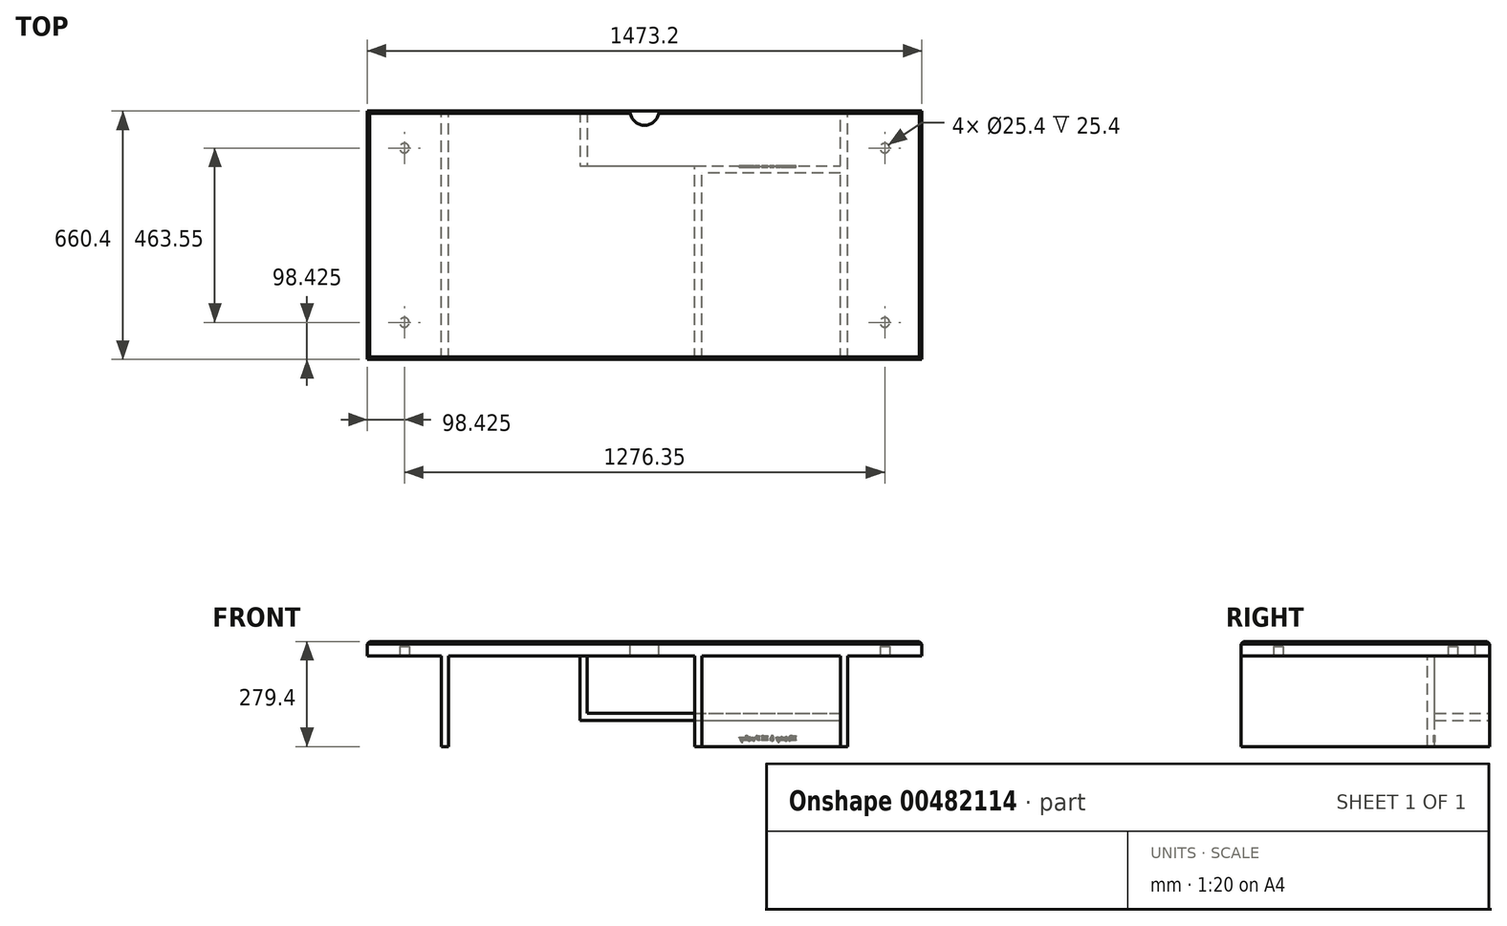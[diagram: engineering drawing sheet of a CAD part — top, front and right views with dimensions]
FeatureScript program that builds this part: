
annotation { "Feature Type Name" : "Feature", "Feature Type Description" : "" }
export const myFeature = defineFeature(function(context is Context, id is Id, definition is map)
    precondition{}
    {
        {
            var Q0;
            Q0=qCreatedBy(makeId("Top.planeOp"),FACE);
            var sketch = newSketch(context, id + "F0", { "sketchPlane" : qUnion([Q0])});
            skLineSegment(sketch, "E0.bottom", {"start": v(-736.6, 330.2) * mm, "end": v(736.6, 330.2) * mm});
            skLineSegment(sketch, "E0.top", {"start": v(-736.6, -330.2) * mm, "end": v(736.6, -330.2) * mm});
            skLineSegment(sketch, "E0.left", {"start": v(-736.6, 330.2) * mm, "end": v(-736.6, -330.2) * mm});
            skLineSegment(sketch, "E0.right", {"start": v(736.6, 330.2) * mm, "end": v(736.6, -330.2) * mm});
            skPoint(sketch, "E0.middle", {"position": v(0, 0) * mm});
            skSolve(sketch);
        }
        {
            var Q0;
            Q0=qSketchRegion(id+"F0",true);
            extrude(context, id + "F1", {"entities" : qUnion([Q0]), "oppositeDirection" : true, "depth" : 31.75 * mm, "hasSecondDirection" : true, "secondDirectionOppositeDirection" : false, "secondDirectionDepth" : 6.35 * mm});
        }
        {
            var Q0;
            Q0=makeQuery(id+"F1.opExtrude","CAP_FACE",FACE,{"disambiguationData":[OSD([sQuery(id+"F0.wireOp",EDGE,"E0.bottom"),sQuery(id+"F0.wireOp",EDGE,"E0.top"),sQuery(id+"F0.wireOp",EDGE,"E0.left"),sQuery(id+"F0.wireOp",EDGE,"E0.right")])],"isStart":true});
            var sketch = newSketch(context, id + "F2", { "sketchPlane" : qUnion([Q0])});
            skCircle(sketch, "E1", {"center": v(0, 330.2) * mm, "radius": 38.1 * mm});
            skSolve(sketch);
        }
        {
            var Q0;
            Q0=qSketchRegion(id+"F2",true);
            extrude(context, id + "F3", {"entities" : qUnion([Q0]), "operationType" : NewBodyOperationType.REMOVE, "endBound" : BoundingType.THROUGH_ALL, "oppositeDirection" : true, "depth" : 25.4 * mm});
        }
        {
            var Q0;
            Q0=makeQuery(id+"F1.opExtrude","CAP_FACE",FACE,{"disambiguationData":[OSD([sQuery(id+"F0.wireOp",EDGE,"E0.bottom"),sQuery(id+"F0.wireOp",EDGE,"E0.top"),sQuery(id+"F0.wireOp",EDGE,"E0.left"),sQuery(id+"F0.wireOp",EDGE,"E0.right")])],"isStart":false});
            var sketch = newSketch(context, id + "F4", { "sketchPlane" : qUnion([Q0])});
            skLineSegment(sketch, "E2.bottom", {"start": v(-539.75, 330.2) * mm, "end": v(-520.7, 330.2) * mm});
            skLineSegment(sketch, "E2.top", {"start": v(-539.75, -330.2) * mm, "end": v(-520.7, -330.2) * mm});
            skLineSegment(sketch, "E2.left", {"start": v(-539.75, 330.2) * mm, "end": v(-539.75, -330.2) * mm});
            skLineSegment(sketch, "E2.right", {"start": v(-520.7, 330.2) * mm, "end": v(-520.7, -330.2) * mm});
            skPoint(sketch, "E3.oppositeSnap0", {"position": v(-530.23, -330.2) * mm});
            skSolve(sketch);
        }
        {
            var Q0;
            Q0=qSketchRegion(id+"F4",true);
            extrude(context, id + "F5", {"entities" : qUnion([Q0]), "operationType" : NewBodyOperationType.ADD, "flatOperationType" : FlatOperationType.REMOVE, "offsetDistance" : 25.4 * mm, "depth" : 241.3 * mm, "domain" : OperationDomain.MODEL});
        }
        {
            var Q0;
            {var subQ0=sQuery(id+"F0.wireOp",EDGE,"E0.bottom");var subQ1=sQuery(id+"F0.wireOp",EDGE,"E0.right");Q0=makeQuery(id+"F3.boolean.opBoolean","SPLIT",EDGE,{"disambiguationData":[TD([makeQuery(id+"F1.opExtrude","SWEPT_FACE",FACE,{"disambiguationData":[OSD([subQ1])]})])],"derivedFrom":makeQuery(id+"F1.opExtrude","CAP_EDGE",EDGE,{"disambiguationData":[OSD([subQ0])],"isStart":true})});}
            var Q1;
            Q1=makeQuery(id+"F1.opExtrude","CAP_EDGE",EDGE,{"disambiguationData":[OSD([sQuery(id+"F0.wireOp",EDGE,"E0.right")])],"isStart":true});
            var Q2;
            {var subQ0=sQuery(id+"F0.wireOp",EDGE,"E0.bottom");var subQ1=sQuery(id+"F0.wireOp",EDGE,"E0.left");Q2=makeQuery(id+"F3.boolean.opBoolean","SPLIT",EDGE,{"disambiguationData":[TD([makeQuery(id+"F1.opExtrude","SWEPT_FACE",FACE,{"disambiguationData":[OSD([subQ1])]})])],"derivedFrom":makeQuery(id+"F1.opExtrude","CAP_EDGE",EDGE,{"disambiguationData":[OSD([subQ0])],"isStart":true})});}
            var Q3;
            Q3=makeQuery(id+"F1.opExtrude","CAP_EDGE",EDGE,{"disambiguationData":[OSD([sQuery(id+"F0.wireOp",EDGE,"E0.left")])],"isStart":true});
            var Q4;
            Q4=makeQuery(id+"F1.opExtrude","CAP_EDGE",EDGE,{"disambiguationData":[OSD([sQuery(id+"F0.wireOp",EDGE,"E0.top")])],"isStart":true});
            var Q5;
            Q5=makeQuery(id+"F3.boolean.opBoolean","COPY",EDGE,{"derivedFrom":makeQuery(id+"F3.opExtrude","CAP_EDGE",EDGE,{"disambiguationData":[OSD([sQuery(id+"F2.wireOp",EDGE,"E1")])],"isStart":true})});
            chamfer(context, id + "F6", {"entities" : qUnion([Q0, Q1, Q2, Q3, Q4, Q5]), "width" : 6.35 * mm, "tangentPropagation" : true});
        }
        {
            var Q0;
            Q0=makeQuery(id+"F1.opExtrude","CAP_FACE",FACE,{"disambiguationData":[OSD([sQuery(id+"F0.wireOp",EDGE,"E0.bottom"),sQuery(id+"F0.wireOp",EDGE,"E0.top"),sQuery(id+"F0.wireOp",EDGE,"E0.left"),sQuery(id+"F0.wireOp",EDGE,"E0.right")])],"isStart":false});
            var sketch = newSketch(context, id + "F7", { "sketchPlane" : qUnion([Q0])});
            skCircle(sketch, "E4", {"center": v(-638.18, 231.77) * mm, "radius": 12.7 * mm});
            skCircle(sketch, "E5", {"center": v(-638.18, -231.78) * mm, "radius": 12.7 * mm});
            skCircle(sketch, "E6", {"center": v(638.18, 231.78) * mm, "radius": 12.7 * mm});
            skCircle(sketch, "E7", {"center": v(638.18, -231.78) * mm, "radius": 12.7 * mm});
            skLineSegment(sketch, "E8", {"start": v(-638.18, 231.77) * mm, "end": v(-736.6, 231.77) * mm, "construction": true});
            skLineSegment(sketch, "E9", {"start": v(-539.75, 231.77) * mm, "end": v(-638.18, 231.77) * mm, "construction": true});
            skLineSegment(sketch, "E10", {"start": v(-638.18, 231.77) * mm, "end": v(-638.18, 330.2) * mm, "construction": true});
            skPoint(sketch, "E10.endSnap0", {"position": v(-638.18, 330.2) * mm});
            skLineSegment(sketch, "E11", {"start": v(-736.6, -231.78) * mm, "end": v(-638.18, -231.78) * mm, "construction": true});
            skLineSegment(sketch, "E12", {"start": v(-638.18, -231.78) * mm, "end": v(-638.18, -330.2) * mm, "construction": true});
            skLineSegment(sketch, "E13", {"start": v(638.18, -231.78) * mm, "end": v(736.6, -231.78) * mm, "construction": true});
            skLineSegment(sketch, "E14", {"start": v(638.18, -231.78) * mm, "end": v(638.18, -330.2) * mm, "construction": true});
            skLineSegment(sketch, "E15", {"start": v(638.18, 231.78) * mm, "end": v(736.6, 231.78) * mm, "construction": true});
            skLineSegment(sketch, "E16", {"start": v(638.18, 231.78) * mm, "end": v(638.18, 330.2) * mm, "construction": true});
            skSolve(sketch);
        }
        {
            var Q0;
            Q0=qSketchRegion(id+"F7",true);
            extrude(context, id + "F8", {"entities" : qUnion([Q0]), "operationType" : NewBodyOperationType.REMOVE, "oppositeDirection" : true, "depth" : 25.4 * mm});
        }
        {
            var Q0;
            Q0=makeQuery(id+"F1.opExtrude","CAP_FACE",FACE,{"disambiguationData":[OSD([sQuery(id+"F0.wireOp",EDGE,"E0.bottom"),sQuery(id+"F0.wireOp",EDGE,"E0.top"),sQuery(id+"F0.wireOp",EDGE,"E0.left"),sQuery(id+"F0.wireOp",EDGE,"E0.right")])],"isStart":false});
            var sketch = newSketch(context, id + "F9", { "sketchPlane" : qUnion([Q0])});
            skLineSegment(sketch, "E17.bottom", {"start": v(133.35, 330.2) * mm, "end": v(152.4, 330.2) * mm});
            skLineSegment(sketch, "E17.top", {"start": v(133.35, -184.15) * mm, "end": v(152.4, -184.15) * mm});
            skLineSegment(sketch, "E17.left", {"start": v(133.35, 330.2) * mm, "end": v(133.35, -184.15) * mm});
            skLineSegment(sketch, "E17.right", {"start": v(152.4, 330.2) * mm, "end": v(152.4, -165.1) * mm});
            skLineSegment(sketch, "E18.bottom", {"start": v(520.7, 330.2) * mm, "end": v(539.75, 330.2) * mm});
            skLineSegment(sketch, "E18.left", {"start": v(520.7, 330.2) * mm, "end": v(520.7, -165.1) * mm});
            skLineSegment(sketch, "E18.right", {"start": v(539.75, 330.2) * mm, "end": v(539.75, -184.15) * mm});
            skLineSegment(sketch, "E19", {"start": v(520.7, -184.15) * mm, "end": v(133.35, -184.15) * mm});
            skLineSegment(sketch, "E20", {"start": v(520.7, -165.1) * mm, "end": v(152.4, -165.1) * mm});
            skLineSegment(sketch, "E21", {"start": v(539.75, -184.15) * mm, "end": v(539.75, -330.2) * mm});
            skLineSegment(sketch, "E22", {"start": v(539.75, -330.2) * mm, "end": v(520.7, -330.2) * mm});
            skLineSegment(sketch, "E23", {"start": v(520.7, -330.2) * mm, "end": v(520.7, -184.15) * mm});
            skSolve(sketch);
        }
        {
            var Q0;
            Q0=qSketchRegion(id+"F9",true);
            extrude(context, id + "F10", {"entities" : qUnion([Q0]), "operationType" : NewBodyOperationType.ADD, "flatOperationType" : FlatOperationType.REMOVE, "offsetDistance" : 25.4 * mm, "depth" : 241.3 * mm, "domain" : OperationDomain.MODEL});
        }
        {
            var Q0;
            {var subQ0=sQuery(id+"F0.wireOp",EDGE,"E0.bottom");var subQ1=sQuery(id+"F0.wireOp",EDGE,"E0.right");var subQ2=sQuery(id+"F0.wireOp",EDGE,"E0.top");var subQ3=sQuery(id+"F0.wireOp",EDGE,"E0.left");Q0=makeQuery(id+"F10.boolean.opBoolean","SPLIT",FACE,{"disambiguationData":[TD([makeQuery(id+"F1.opExtrude","SWEPT_FACE",FACE,{"disambiguationData":[OSD([subQ0])]})])],"derivedFrom":makeQuery(id+"F1.opExtrude","CAP_FACE",FACE,{"disambiguationData":[OSD([subQ0,subQ2,subQ3,subQ1])],"isStart":false})});}
            var sketch = newSketch(context, id + "F11", { "sketchPlane" : qUnion([Q0])});
            skLineSegment(sketch, "E24.bottom", {"start": v(-171.45, -330.2) * mm, "end": v(-152.4, -330.2) * mm});
            skLineSegment(sketch, "E24.top", {"start": v(-171.45, -184.15) * mm, "end": v(-152.4, -184.15) * mm});
            skLineSegment(sketch, "E24.left", {"start": v(-171.45, -330.2) * mm, "end": v(-171.45, -184.15) * mm});
            skLineSegment(sketch, "E24.right", {"start": v(-152.4, -330.2) * mm, "end": v(-152.4, -184.15) * mm});
            skSolve(sketch);
        }
        {
            var Q0;
            Q0=qSketchRegion(id+"F11",true);
            extrude(context, id + "F12", {"entities" : qUnion([Q0]), "operationType" : NewBodyOperationType.ADD, "depth" : 152.4 * mm});
        }
        {
            var Q0;
            Q0=makeQuery(id+"F12.opExtrude","CAP_FACE",FACE,{"disambiguationData":[OSD([sQuery(id+"F11.wireOp",EDGE,"E24.bottom"),sQuery(id+"F11.wireOp",EDGE,"E24.top"),sQuery(id+"F11.wireOp",EDGE,"E24.left"),sQuery(id+"F11.wireOp",EDGE,"E24.right")])],"isStart":false});
            var sketch = newSketch(context, id + "F13", { "sketchPlane" : qUnion([Q0])});
            skLineSegment(sketch, "E25.bottom", {"start": v(-171.45, -184.15) * mm, "end": v(520.7, -184.15) * mm});
            skLineSegment(sketch, "E25.top", {"start": v(-171.45, -330.2) * mm, "end": v(520.7, -330.2) * mm});
            skLineSegment(sketch, "E25.left", {"start": v(-171.45, -184.15) * mm, "end": v(-171.45, -330.2) * mm});
            skLineSegment(sketch, "E25.right", {"start": v(520.7, -184.15) * mm, "end": v(520.7, -330.2) * mm});
            skSolve(sketch);
        }
        {
            var Q0;
            Q0=qSketchRegion(id+"F13",true);
            extrude(context, id + "F14", {"entities" : qUnion([Q0]), "operationType" : NewBodyOperationType.ADD, "depth" : 19.05 * mm});
        }
        {
            var Q0;
            {var subQ2=sQuery(id+"F9.wireOp",EDGE,"E19");var subQ3=sQuery(id+"F13.wireOp",EDGE,"E25.bottom");Q0=makeQuery(id+"F14.boolean.opBoolean","SPLIT",FACE,{"disambiguationData":[TD([makeQuery(id+"F14.opExtrude","CAP_FACE",FACE,{"disambiguationData":[OSD([subQ3,sQuery(id+"F13.wireOp",EDGE,"E25.top"),sQuery(id+"F13.wireOp",EDGE,"E25.left"),sQuery(id+"F13.wireOp",EDGE,"E25.right")])],"isStart":false})])],"derivedFrom":makeQuery(id+"F10.opExtrude","SWEPT_FACE",FACE,{"disambiguationData":[OSD([subQ2])]})});}
            var sketch = newSketch(context, id + "F15", { "sketchPlane" : qUnion([Q0])});
            skText(sketch, "E26", { "text": "Ebony & El Pucky", "fontName": "RobotoSlab-Bold.ttf"});
            const initialGuessF15  = {"E26": [-0.40323, -0.25718, 1, 0, 0.01311]};
            skSetInitialGuess(sketch, initialGuessF15);
            skSolve(sketch);
        }
        {
            var Q0;
            Q0 = qSketchRegion(id + "F15", true);
            extrude(context, id + "F16", {"entities" : qUnion([Q0]), "operationType" : NewBodyOperationType.REMOVE, "oppositeDirection" : true, "depth" : 3.17 * mm, "hasDraft" : true, "draftAngle" : 3 * degree});
        }
    });
